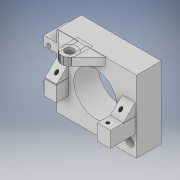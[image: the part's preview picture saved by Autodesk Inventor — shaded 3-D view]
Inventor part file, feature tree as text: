
AUTODESK INVENTOR PART (.ipt)
format: ipt  version: 2017 (Build 210142000, 142)  size: 1,157,120 bytes
history: native  units: in
note: dims shown in document units (in); Inventor stores cm internally (conversion verified against a paired STEP export)
features: projected_geometry x15, extrude x10, sketch x10, imported_body x1
ambient origin geometry x8: Origin, YZ Plane, XZ Plane, XY Plane, X Axis, Y Axis, Z Axis, Center Point
bodies: Solid1 (feature_tree)
feature tree (36):
  extrude  "Extrusion1"  Depth=0.3937in TaperAngle=0.0deg
  extrude  "Extrusion2"  Depth=0.3937in TaperAngle=0.0deg
  extrude  "Extrusion3"  Depth=1.839in
  extrude  "Extrusion4"  Depth=0.327in
  extrude  "Extrusion5"  Depth=0.125in
  extrude  "Extrusion6"  Depth=0.125in
  extrude  "Extrusion7"  Depth=0.5in TaperAngle=0.0deg
  extrude  "Extrusion8"  Depth=0.1562in TaperAngle=0.0deg
  extrude  "Extrusion9"  Depth=0.125in TaperAngle=0.0deg
  extrude  "Extrusion10"  Depth=0.6102in
  sketch  "Sketch1"  dims[d0=0.252in d1=0.3937in d2=0.0in]
  projected_geometry  "Projected Loop1"
  projected_geometry  "Projected Loop2"
  sketch  "Sketch2"  dims[d3=0.3937in d4=0.0in d5=0.625in d6=0.0in]
  projected_geometry  "Projected Loop3"
  sketch  "Sketch3"  dims[d7=0.197in d8=1.839in]
  projected_geometry  "Projected Loop4"
  sketch  "Sketch4"  dims[d9=1.709in d10=0.327in]
  projected_geometry  "Projected Loop5"
  sketch  "Sketch5"  dims[d11=0.125in d12=0.125in]
  projected_geometry  "Projected Loop6"
  sketch  "Sketch6"  dims[d13=0.125in d14=0.0in d15=0.25in]
  projected_geometry  "Projected Loop7"
  sketch  "Sketch7"  dims[d16=0.25in d17=0.5in d18=0.0in]
  projected_geometry  "Projected Loop8"
  sketch  "Sketch9"  dims[d19=0.25in d20=0.1562in d21=0.5in d22=0.0in d23=0.0in]
  projected_geometry  "Projected Loop10"
  projected_geometry  "Projected Loop11"
  projected_geometry  "Projected Loop12"
  projected_geometry  "Projected Loop13"
  projected_geometry  "Projected Loop14"
  sketch  "Sketch10"  dims[d24=1.2992in d25=0.125in d26=0.0in]
  projected_geometry  "Projected Loop15"
  sketch  "Sketch11"  dims[d27=0.0787in d28=0.0in d29=0.6102in d30=0.4528in d31=90.0deg d32=0.2756in d33=0.2756in d34=0.3937in d35=0.0in d39=0.1969in d40=0.0in d44=0.1575in d45=0.1929in d46=0.125in d47=0.1929in d48=0.125in d49=0.1575in]
  projected_geometry  "Projected Loop16"
  imported_body  "Base1"
